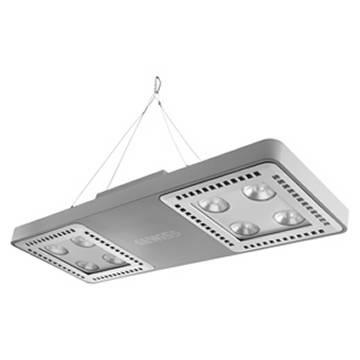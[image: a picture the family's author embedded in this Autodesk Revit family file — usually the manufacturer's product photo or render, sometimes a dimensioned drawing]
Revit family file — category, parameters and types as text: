
# Revit family: Lighting-Industriale-GEWISS-SMART[4]HLO_APPARECCHI-LED_2M_DALI
name_source: partatom
category: Apparecchi per illuminazione
units: mm (PartAtom-declared; Revit-internal decimal feet)

## family parameters
Basato su piano di lavoro = Sì
Condiviso = No
Numero OmniClass = 23.80.70.00
Punto di calcolo locali = No
Quota connettore circolare = Usa diametro
Sempre verticale = No
Sorgente d'illuminazione = No
Taglio con vuoti quando caricato = No
Tipo di parte = Normale
Titolo OmniClass = Lighting

## types (1)
- Lighting-Industriale-GEWISS-SMART[4]HLO_APPARECCHI-LED_2M_DALI
    Alimentatore = Incluso
    Apparecchio a ridotta temperatura superficiale = Si
    Applicazione = Interno
    Cablaggio = Con connettore stagno Gw connect
    Caratteristiche elettriche e gestione della luce = -
    Caratteristiche ottiche e illuminotecniche = -
    Carico apparente = 97 VA
    Catalogo = LIGHTING
    Certificazione DIN 18032-3 = Con Staffa - Kit Funi + morsetto (in approvazione)
    Certificazioni e classificazioni = -
    Classe fotobiologica = RG0
    Classe isolamento = I
    Classificazione = Lighting
    Classificazione: = -
    Codice Electrocod = 2444
    Codice digitale univoco (Datamatrix) = Datamatrix
    Colore = Grigio RAL 7035
    Commenti sul wattaggio = 97W
    Contesto = Illuminazione di industrie e impianti sportivi
    Controllo abbagliamento e luminanza = -
    Corpo = PA6 “Halogen Free” caricato fibra vetro
    Descrizione = SMART[4]HB 2M C.PAS.DALI HLO ELL.57K
    Dispositivo di protezione = DM 6 kV / CM 10 kV
    Dist_sorg_lum = 10 mm  [stored 0.0328084 ft]
    Durata di vita = L90B10 (Tq+25°C) = 100.000 h - L90B10 (Tq+50°C) = 50.000 h
    Efficienza luminosa (lm/W) = 128
    Finitura colore = Grigio RAL 7035
    Fissaggio = -
    Frequenza nominale (Hz) = 50/60 Hz
    Gancio di chiusura = -
    Garanzia = 5 anni
    Grado di protezione = IP66
    Gruppo ottico = Riflettore in PC metallizzato e lenti in PMMA
    Guarnizioni = tipo siliconico antinvecchiamento
    IDF = a8eec59c-6afa-41b9-83ec-62c64bb69aaf
    IDT = 39c294b6b8a14fd39c4f066ec01eb55a
    IPEA = -
    Immagine tipo = GWL1311.jpg
    Inclinazione = Con accessorio staffa
    Indice di resa cromatica = CRI-80
    Informazioni generali = -
    Installazione e manutenzione = -
    Lampada = LED
    Larghezza = 254 mm
    Lumen output (lm) = 16000
    Lunghezza = 699 mm  [stored 2.29331 ft]
    Mascherina = <Per categoria>
    Materiali = -
    Modello = GWS4223BQ857
    Motore = <Per categoria>
    Norma di riferimento = EN 60598-1 ; EN 60598-2-1 ; EN 60598-2-24
    Ottica = Ellittica
    Peso (kg): = 6,5
    Potenza di sistema = 125W
    Produttore = GEWISS S.p.A.
    Prospetto di default = 1219 mm
    Resistenza agli urti = IK08
    Resistenza al filo incandescente = 850 °C
    SEO = High bay
    Scheda Tecnica = https://www.gewiss.com
    Schermo = Vetro Temprato Spessore 4mm
    Sistema di controllo = 1 x DALI DT6
    Sistema di controllo : = DALI
    Sostituibilità gruppo ottico = Non sostituibile
    Sostituibilità piastra di cablaggio = Non sostituibile
    Spessore plafoniera = 40 mm  [stored 0.131234 ft]
    Struttura plafoniera = <Per categoria>
    Superficie massima esposta al vento : = 0,184 m²
    Temperatura di colore = 5700K
    Temperatura di esercizio = -30°C ÷ +50 °C
    Temperatura di stoccaggio = -40 +70 °C
    Tensione di alimentazione = 220 - 240 V
    Tipo di apparecchio = Riflettore industriale a LED&nbsp;
    Tipo di installazione e montaggio = Plafone - Parete - Sospensione
    Tipologia sorgente luminosa = LED - Non sostituibile
    Tolleranza cromatica = SDCM = 3
    Trasformatore = <Per categoria>
    URL = https://www.gewiss.com
    Vano di alimentazione = Integrato
    Versione file RFA = 20.11
    Viti esterne = Acciaio inox
    Voltaggio = 230 V

note: [stored X ft] marks values corroborated as IEEE doubles in the binary element streams (Revit-internal decimal feet)

## geometry (parser evidence)
native form markers: Blend x4, Sweep x3
no freeform markers — native parametric forms only
